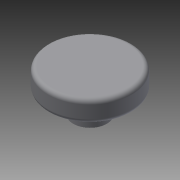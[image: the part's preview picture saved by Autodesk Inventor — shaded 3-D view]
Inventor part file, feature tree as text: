
AUTODESK INVENTOR PART (.ipt)
format: ipt  version: 2015 (Build 190159000, 159)  size: 111,104 bytes
history: native  units: in
note: dims shown in document units (in); Inventor stores cm internally (conversion verified against a paired STEP export)
features: revolve x1, sketch x1
ambient origin geometry x8: Origin, YZ Plane, XZ Plane, XY Plane, X Axis, Y Axis, Z Axis, Center Point
bodies: Solid1 (feature_tree)
feature tree (2):
  revolve  "Revolution1"  [1 undecoded]
  sketch  "Sketch1"  dims[d0=1.0in d1=0.4in d2=0.5in d3=1.0in d4=0.1in d5=90.0deg]
note: 1 required parameter value undecoded (feature->parameter linkage not recoverable at this tier; creation-order binding heuristic only, values carry confidence <= 0.55)
